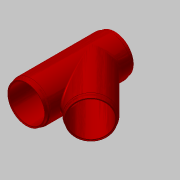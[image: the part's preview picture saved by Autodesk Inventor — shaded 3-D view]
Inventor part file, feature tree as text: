
AUTODESK INVENTOR PART (.ipt)
format: ipt  version: 2017.3 (Build 213257000, 257)  size: 336,896 bytes
history: native  units: in
note: dims shown in document units (in); Inventor stores cm internally (conversion verified against a paired STEP export)
features: extrude x18, sketch x14, fillet x6, chamfer x3, plane x1
ambient origin geometry x8: Origin, YZ Plane, XZ Plane, XY Plane, X Axis, Y Axis, Z Axis, Center Point
bodies: Solid1 (feature_tree)
feature tree (42):
  sketch  "Sketch1"  dims[d0=28.5in d1=31.0in]
  extrude  "Extrusion1"  Depth=31.0in
  plane  "Work Plane1"
  sketch  "Sketch2"  dims[d2=33.0in d3=52.9606in d4=19.4961in d5=0.0in d6=0.0in]
  extrude  "Extrusion2"  Depth=52.9606in TaperAngle=0.0deg
  extrude  "Extrusion3"  Depth=28.5in
  extrude  "Extrusion4"  Depth=33.0in
  extrude  "Extrusion5"  Depth=52.9606in
  extrude  "Extrusion6"  Depth=0.5in
  extrude  "Extrusion7"  TaperAngle=0.0deg  [1 undecoded]
  extrude  "Extrusion8"  Depth=0.5in
  extrude  "Extrusion9"  Depth=49.9606in
  fillet  "Fillet1"  Radius=16.4961in
  fillet  "Fillet2"  [1 undecoded]
  fillet  "Fillet3"  Radius=49.9606in
  fillet  "Fillet4"  [1 undecoded]
  extrude  "Extrusion10"  TaperAngle=0.0deg  [1 undecoded]
  extrude  "Extrusion11"  TaperAngle=0.0deg  [1 undecoded]
  extrude  "Extrusion12"  Depth=6.0in
  fillet  "Fillet5"  Radius=1.0in
  chamfer  "Chamfer2"  Distance=1.0in
  fillet  "Fillet6"  Radius=32.48in
  chamfer  "Chamfer3"  Distance=1.0in
  extrude  "Extrusion13"  Depth=0.0312in
  extrude  "Extrusion14"  Depth=0.0312in TaperAngle=0.0deg
  extrude  "Extrusion15"  Depth=0.0312in
  chamfer  "Chamfer4"  Distance=0.74in
  extrude  "Extrusion16"  Depth=0.0312in TaperAngle=45.0deg
  extrude  "Extrusion17"  Depth=0.0312in
  extrude  "Extrusion18"  Depth=0.0312in TaperAngle=45.0deg
  sketch  "Sketch3"  dims[d7=45.0deg d8=28.5in]
  sketch  "Sketch4"  dims[d9=31.0in d10=33.0in]
  sketch  "Sketch5"  dims[d11=52.9606in d12=0.0in d13=30.0in]
  sketch  "Sketch6"  dims[d14=0.5in d15=0.0in d16=30.0in]
  sketch  "Sketch7"  dims[d17=0.5in d18=0.0in]
  sketch  "Sketch8"  dims[d19=30.0in d20=0.5in]
  sketch  "Sketch9"  dims[d21=0.0in d22=49.9606in d23=16.4961in d24=0.0in d25=0.0in d26=49.9606in d27=0.0in]
  sketch  "Sketch10"  dims[d28=52.9606in d29=0.0in]
  sketch  "Sketch11"  dims[d30=52.9606in d31=0.0in]
  sketch  "Sketch12"  dims[d32=1.0in d33=6.0in d34=1.0in]
  sketch  "Sketch13"  dims[d35=1.0in]
  sketch  "Sketch14"  dims[d39=32.48in d40=1.0in d41=0.0in d42=32.48in d43=1.0in d44=0.0in d45=32.48in d46=1.0in d47=0.0in d48=0.0312in d49=0.74in d50=0.125in d51=45.0deg d52=0.0312in d53=0.0312in d54=0.125in d55=45.0deg d56=1.0in d57=0.0in d58=1.0in d59=0.0in d60=1.0in d61=0.0in d62=0.26in d64=0.125in d65=45.0deg d66=1.0in d67=0.0in d68=1.0in d69=0.0in d70=1.0in d71=0.0in]
note: 5 required parameter values undecoded (feature->parameter linkage not recoverable at this tier; creation-order binding heuristic only, values carry confidence <= 0.55)
